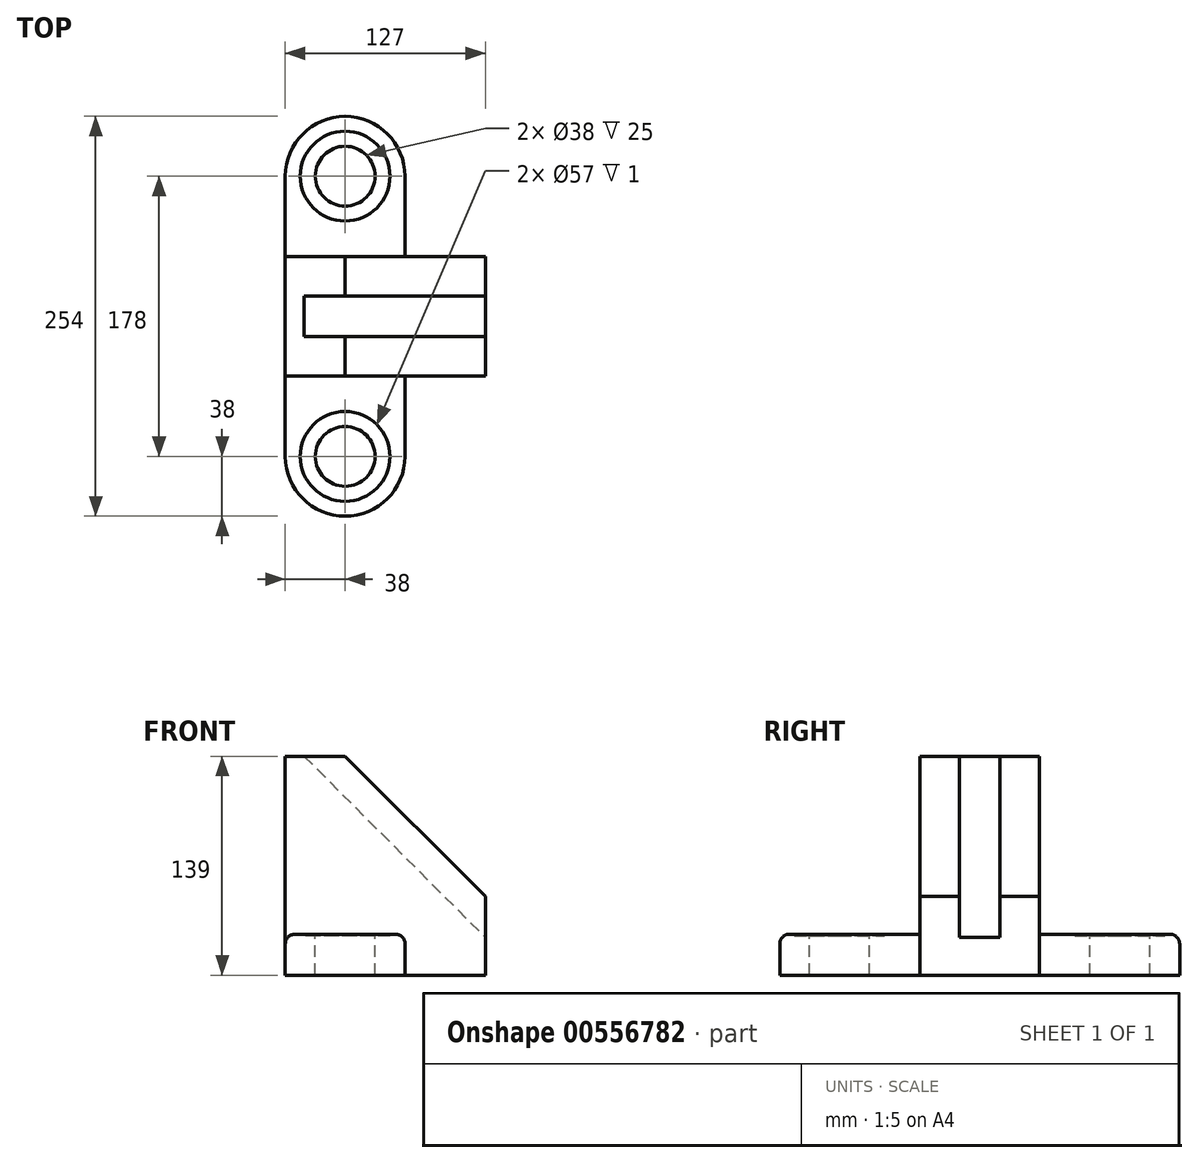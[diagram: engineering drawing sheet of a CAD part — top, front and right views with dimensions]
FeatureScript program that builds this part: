
annotation { "Feature Type Name" : "Feature", "Feature Type Description" : "" }
export const myFeature = defineFeature(function(context is Context, id is Id, definition is map)
    precondition{}
    {
        {
            var Q0;
            Q0=qCreatedBy(makeId("Front.planeOp"),FACE);
            var sketch = newSketch(context, id + "F0", { "sketchPlane" : qUnion([Q0])});
            skLineSegment(sketch, "E0", {"start": v(0, 0) * mm, "end": v(127, 0) * mm});
            skLineSegment(sketch, "E1", {"start": v(127, 0) * mm, "end": v(127, 50) * mm});
            skLineSegment(sketch, "E2", {"start": v(0, 0) * mm, "end": v(0, 139) * mm});
            skLineSegment(sketch, "E3", {"start": v(127, 50) * mm, "end": v(18.66, 158.34) * mm});
            skLineSegment(sketch, "E4", {"start": v(0, 139) * mm, "end": v(38, 139) * mm});
            skSolve(sketch);
        }
        {
            var Q0;
            Q0 = qSketchRegion(id + "F0", true);
            extrude(context, id + "F1", {"entities" : qUnion([Q0]), "endBound" : BoundingType.SYMMETRIC, "depth" : 76 * mm, "offsetDistance" : 25 * mm});
        }
        {
            var Q0;
            Q0=makeQuery(id+"F1.opExtrude","SWEPT_FACE",FACE,{"disambiguationData":[OSD([sQuery(id+"F0.wireOp",EDGE,"E0")])]});
            var sketch = newSketch(context, id + "F2", { "sketchPlane" : qUnion([Q0])});
            skLineSegment(sketch, "E5", {"start": v(38, -89) * mm, "end": v(38, 89) * mm, "construction": true});
            skLineSegment(sketch, "E6", {"start": v(0, 0) * mm, "end": v(133.16, 0) * mm, "construction": true});
            skPoint(sketch, "E6.endSnap0", {"position": v(127, 0) * mm});
            skArc(sketch, "E7.0.startCap", {"start": v(76, -89) * mm, "mid": v(38, -127) * mm, "end": v(0, -89) * mm});
            skArc(sketch, "E7.0.endCap", {"start": v(0, 89) * mm, "mid": v(38, 127) * mm, "end": v(76, 89) * mm});
            skLineSegment(sketch, "E7.0.left", {"start": v(0, -89) * mm, "end": v(0, 89) * mm});
            skLineSegment(sketch, "E7.0.right", {"start": v(76, -89) * mm, "end": v(76, 89) * mm});
            skSolve(sketch);
        }
        {
            var Q0;
            Q0=qCreatedBy(makeId("Front.planeOp"),FACE);
            var sketch = newSketch(context, id + "F3", { "sketchPlane" : qUnion([Q0])});
            skLineSegment(sketch, "E8", {"start": v(38, 139) * mm, "end": v(12, 139) * mm});
            skLineSegment(sketch, "E9", {"start": v(38, 139) * mm, "end": v(127, 50) * mm});
            skLineSegment(sketch, "E10", {"start": v(12, 139) * mm, "end": v(127, 24) * mm});
            skLineSegment(sketch, "E11", {"start": v(127, 50) * mm, "end": v(127, 24) * mm});
            skSolve(sketch);
        }
        {
            var Q0;
            Q0 = qSketchRegion(id + "F3", true);
            extrude(context, id + "F4", {"entities" : qUnion([Q0]), "operationType" : NewBodyOperationType.REMOVE, "endBound" : BoundingType.SYMMETRIC, "oppositeDirection" : true, "depth" : 26 * mm, "offsetDistance" : 25 * mm});
        }
        {
            var Q0;
            Q0 = qSketchRegion(id + "F2", true);
            extrude(context, id + "F5", {"entities" : qUnion([Q0]), "operationType" : NewBodyOperationType.ADD, "oppositeDirection" : true, "depth" : 26 * mm, "offsetDistance" : 25 * mm});
        }
        {
            var Q0;
            {var subQ0=sQuery(id+"F2.wireOp",EDGE,"E7.0.left");var subQ1=sQuery(id+"F2.wireOp",EDGE,"E7.0.endCap");var subQ3=sQuery(id+"F2.wireOp",EDGE,"E7.0.right");Q0=makeQuery(id+"F5.boolean.opBoolean","SPLIT",FACE,{"disambiguationData":[TD([makeQuery(id+"F5.opExtrude","SWEPT_FACE",FACE,{"disambiguationData":[OSD([subQ1])]})])],"derivedFrom":makeQuery(id+"F5.opExtrude","CAP_FACE",FACE,{"disambiguationData":[OSD([sQuery(id+"F2.wireOp",EDGE,"E7.0.startCap"),subQ1,subQ0,subQ3])],"isStart":false})});}
            var sketch = newSketch(context, id + "F6", { "sketchPlane" : qUnion([Q0])});
            skLineSegment(sketch, "E12", {"start": v(0, -89) * mm, "end": v(76, -89) * mm, "construction": true});
            skLineSegment(sketch, "E13", {"start": v(38, -127) * mm, "end": v(38, -66.67) * mm, "construction": true});
            skCircle(sketch, "E14", {"center": v(38, -89) * mm, "radius": 19 * mm});
            skSolve(sketch);
        }
        {
            var Q0;
            Q0 = qSketchRegion(id + "F6", true);
            extrude(context, id + "F7", {"entities" : qUnion([Q0]), "operationType" : NewBodyOperationType.REMOVE, "endBound" : BoundingType.THROUGH_ALL, "oppositeDirection" : true, "depth" : 25 * mm, "offsetDistance" : 25 * mm});
        }
        {
            var Q0;
            {var subQ0=sQuery(id+"F2.wireOp",EDGE,"E7.0.left");var subQ1=sQuery(id+"F2.wireOp",EDGE,"E7.0.endCap");var subQ3=sQuery(id+"F2.wireOp",EDGE,"E7.0.right");Q0=makeQuery(id+"F5.boolean.opBoolean","SPLIT",FACE,{"disambiguationData":[TD([makeQuery(id+"F5.opExtrude","SWEPT_FACE",FACE,{"disambiguationData":[OSD([subQ1])]})])],"derivedFrom":makeQuery(id+"F5.opExtrude","CAP_FACE",FACE,{"disambiguationData":[OSD([sQuery(id+"F2.wireOp",EDGE,"E7.0.startCap"),subQ1,subQ0,subQ3])],"isStart":false})});}
            var sketch = newSketch(context, id + "F8", { "sketchPlane" : qUnion([Q0])});
            skLineSegment(sketch, "E15", {"start": v(0, -89) * mm, "end": v(76, -89) * mm, "construction": true});
            skLineSegment(sketch, "E16", {"start": v(38, -127) * mm, "end": v(38, -62.55) * mm, "construction": true});
            skCircle(sketch, "E17", {"center": v(38, -89) * mm, "radius": 28.5 * mm});
            skSolve(sketch);
        }
        {
            var Q0;
            Q0 = qSketchRegion(id + "F8", true);
            extrude(context, id + "F9", {"entities" : qUnion([Q0]), "operationType" : NewBodyOperationType.REMOVE, "oppositeDirection" : true, "depth" : 1 * mm, "offsetDistance" : 25 * mm});
        }
        {
            var Q0;
            {var subQ0=sQuery(id+"F2.wireOp",EDGE,"E7.0.startCap");var subQ2=sQuery(id+"F2.wireOp",EDGE,"E7.0.left");var subQ3=sQuery(id+"F2.wireOp",EDGE,"E7.0.right");Q0=makeQuery(id+"F5.boolean.opBoolean","SPLIT",FACE,{"disambiguationData":[TD([makeQuery(id+"F5.opExtrude","SWEPT_FACE",FACE,{"disambiguationData":[OSD([subQ0])]})])],"derivedFrom":makeQuery(id+"F5.opExtrude","CAP_FACE",FACE,{"disambiguationData":[OSD([subQ0,sQuery(id+"F2.wireOp",EDGE,"E7.0.endCap"),subQ2,subQ3])],"isStart":false})});}
            var sketch = newSketch(context, id + "F10", { "sketchPlane" : qUnion([Q0])});
            skLineSegment(sketch, "E18", {"start": v(0, 89) * mm, "end": v(76, 89) * mm, "construction": true});
            skLineSegment(sketch, "E19", {"start": v(38, 127) * mm, "end": v(38, 68.58) * mm, "construction": true});
            skPoint(sketch, "E19.endSnap0", {"position": v(38, 127) * mm});
            skCircle(sketch, "E20", {"center": v(38, 89) * mm, "radius": 19 * mm});
            skSolve(sketch);
        }
        {
            var Q0;
            Q0 = qSketchRegion(id + "F10", true);
            extrude(context, id + "F11", {"entities" : qUnion([Q0]), "operationType" : NewBodyOperationType.REMOVE, "endBound" : BoundingType.THROUGH_ALL, "oppositeDirection" : true, "depth" : 25 * mm, "offsetDistance" : 25 * mm});
        }
        {
            var Q0;
            {var subQ0=sQuery(id+"F2.wireOp",EDGE,"E7.0.startCap");var subQ2=sQuery(id+"F2.wireOp",EDGE,"E7.0.left");var subQ3=sQuery(id+"F2.wireOp",EDGE,"E7.0.right");Q0=makeQuery(id+"F5.boolean.opBoolean","SPLIT",FACE,{"disambiguationData":[TD([makeQuery(id+"F5.opExtrude","SWEPT_FACE",FACE,{"disambiguationData":[OSD([subQ0])]})])],"derivedFrom":makeQuery(id+"F5.opExtrude","CAP_FACE",FACE,{"disambiguationData":[OSD([subQ0,sQuery(id+"F2.wireOp",EDGE,"E7.0.endCap"),subQ2,subQ3])],"isStart":false})});}
            var sketch = newSketch(context, id + "F12", { "sketchPlane" : qUnion([Q0])});
            skLineSegment(sketch, "E21", {"start": v(0, 89) * mm, "end": v(76, 89) * mm, "construction": true});
            skLineSegment(sketch, "E22", {"start": v(38, 127) * mm, "end": v(38, 54.3) * mm, "construction": true});
            skPoint(sketch, "E22.endSnap0", {"position": v(38, 127) * mm});
            skCircle(sketch, "E23", {"center": v(38, 89) * mm, "radius": 28.5 * mm});
            skSolve(sketch);
        }
        {
            var Q0;
            Q0 = qSketchRegion(id + "F12", true);
            extrude(context, id + "F13", {"entities" : qUnion([Q0]), "operationType" : NewBodyOperationType.REMOVE, "oppositeDirection" : true, "depth" : 1 * mm, "offsetDistance" : 25 * mm});
        }
        {
            var Q0;
            {var subQ0=sQuery(id+"F2.wireOp",EDGE,"E7.0.right");var subQ1=sQuery(id+"F2.wireOp",EDGE,"E7.0.endCap");Q0=makeQuery(id+"F5.boolean.opBoolean","SPLIT",EDGE,{"disambiguationData":[TD([makeQuery(id+"F5.opExtrude","SWEPT_FACE",FACE,{"disambiguationData":[OSD([subQ1])]})])],"derivedFrom":makeQuery(id+"F5.opExtrude","CAP_EDGE",EDGE,{"disambiguationData":[OSD([subQ0])],"isStart":false})});}
            var Q1;
            {var subQ0=sQuery(id+"F2.wireOp",EDGE,"E7.0.endCap");var subQ1=sQuery(id+"F2.wireOp",EDGE,"E7.0.left");Q1=makeQuery(id+"F5.boolean.opBoolean","SPLIT",EDGE,{"disambiguationData":[TD([makeQuery(id+"F5.opExtrude","SWEPT_FACE",FACE,{"disambiguationData":[OSD([subQ0])]})])],"derivedFrom":makeQuery(id+"F5.opExtrude","CAP_EDGE",EDGE,{"disambiguationData":[OSD([subQ1])],"isStart":false})});}
            var Q2;
            Q2=makeQuery(id+"F5.opExtrude","CAP_EDGE",EDGE,{"disambiguationData":[OSD([sQuery(id+"F2.wireOp",EDGE,"E7.0.endCap")])],"isStart":false});
            var Q3;
            {var subQ0=sQuery(id+"F2.wireOp",EDGE,"E7.0.startCap");var subQ1=sQuery(id+"F2.wireOp",EDGE,"E7.0.right");Q3=makeQuery(id+"F5.boolean.opBoolean","SPLIT",EDGE,{"disambiguationData":[TD([makeQuery(id+"F5.opExtrude","SWEPT_FACE",FACE,{"disambiguationData":[OSD([subQ0])]})])],"derivedFrom":makeQuery(id+"F5.opExtrude","CAP_EDGE",EDGE,{"disambiguationData":[OSD([subQ1])],"isStart":false})});}
            var Q4;
            Q4=makeQuery(id+"F5.opExtrude","CAP_EDGE",EDGE,{"disambiguationData":[OSD([sQuery(id+"F2.wireOp",EDGE,"E7.0.startCap")])],"isStart":false});
            var Q5;
            {var subQ0=sQuery(id+"F2.wireOp",EDGE,"E7.0.startCap");var subQ1=sQuery(id+"F2.wireOp",EDGE,"E7.0.left");Q5=makeQuery(id+"F5.boolean.opBoolean","SPLIT",EDGE,{"disambiguationData":[TD([makeQuery(id+"F5.opExtrude","SWEPT_FACE",FACE,{"disambiguationData":[OSD([subQ0])]})])],"derivedFrom":makeQuery(id+"F5.opExtrude","CAP_EDGE",EDGE,{"disambiguationData":[OSD([subQ1])],"isStart":false})});}
            fillet(context, id + "F14", {"entities" : qUnion([Q0, Q1, Q2, Q3, Q4, Q5]), "radius" : 6 * mm, "tangentPropagation" : true, "allowEdgeOverflow" : false});
        }
    });
